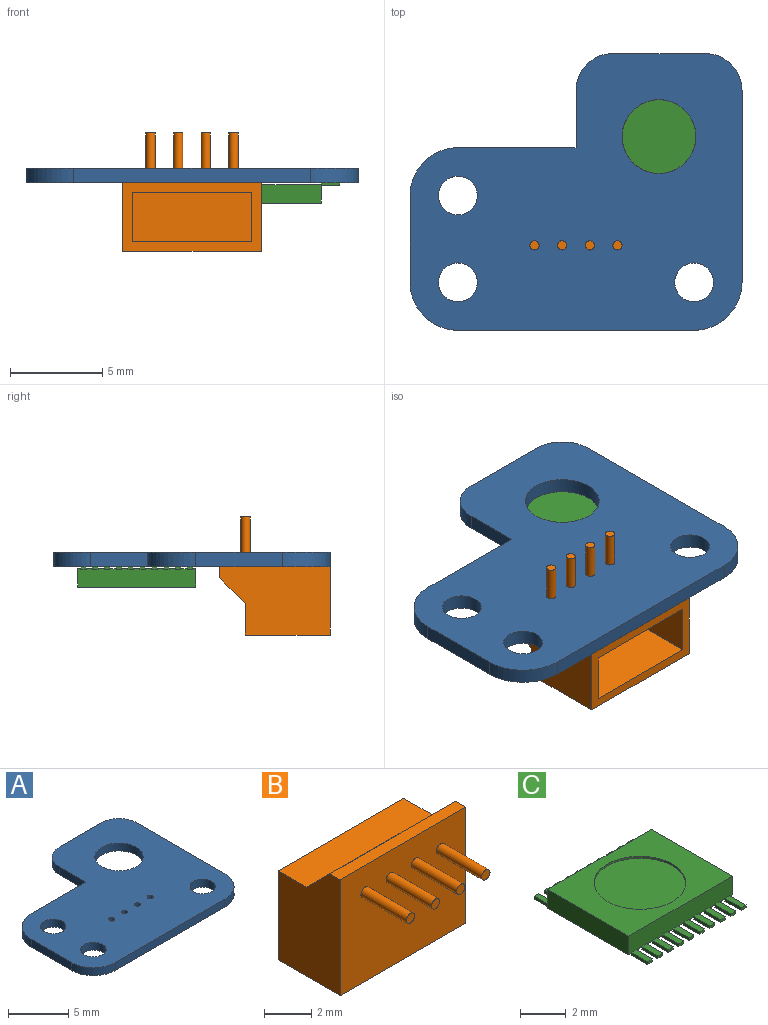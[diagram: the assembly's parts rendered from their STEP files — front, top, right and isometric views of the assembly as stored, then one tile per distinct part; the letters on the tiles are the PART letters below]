
ASSEMBLY  parts=3 mates=3
PART A: 21 faces, bbox 18x15x0.8 mm
  f0: plane 5x0.8mm, normal (0,1,0), area 4mm2, adj f4,f5,f19,f20
  f1: plane 4.7x0.8mm, normal (-1,0,0), area 3.8mm2, adj f4,f5,f16,f17
  f2: plane 12.8x0.8mm, normal (0,-1,0), area 10.2mm2, adj f4,f5,f17,f18
  f3: plane 10.4x0.8mm, normal (1,0,0), area 8.3mm2, adj f4,f5,f18,f20
  f4: plane 18x15mm, normal (0,0,1), area 194.3mm2, adj f0,f1,f2,f3,f6,f7,f8,f9
  f5: plane 18x15mm, normal (0,0,-1), area 194.3mm2, adj f0,f1,f2,f3,f6,f7,f8,f9
  f6: cylinder r=0.25mm len=0.8mm, axis (0,0,-1), area 1.3mm2, adj f4,f5
  f7: cylinder r=0.25mm len=0.8mm, axis (0,0,-1), area 1.3mm2, adj f4,f5
  f8: cylinder r=0.25mm len=0.8mm, axis (0,0,-1), area 1.3mm2, adj f4,f5
  f9: cylinder r=0.25mm len=0.8mm, axis (0,0,-1), area 1.3mm2, adj f4,f5
  f10: cylinder r=1.05mm len=2.1mm, axis (0,0,1), area 5.3mm2, adj f4,f5
  f11: cylinder r=1.05mm len=2.1mm, axis (0,0,1), area 5.3mm2, adj f4,f5
  f12: cylinder r=1.05mm len=2.1mm, axis (0,0,1), area 5.3mm2, adj f4,f5
  f13: plane 6.4x0.8mm, normal (0,1,0), area 5.1mm2, adj f4,f5,f14,f16
  f14: plane 3.1x0.8mm, normal (-1,0,0), area 2.5mm2, adj f4,f5,f13,f19
  f15: cylinder r=2mm len=4mm, axis (0,0,-1), area 10.1mm2, adj f4,f5
  f16: cylinder r=2.6mm len=2.6mm, axis (0,0,-1), area 3.3mm2, adj f1,f4,f5,f13
  f17: cylinder r=2.6mm len=2.6mm, axis (0,0,1), area 3.3mm2, adj f1,f2,f4,f5
  f18: cylinder r=2.6mm len=2.6mm, axis (0,0,-1), area 3.3mm2, adj f2,f3,f4,f5
  f19: cylinder r=2mm len=2mm, axis (0,0,1), area 2.5mm2, adj f0,f4,f5,f14
  f20: cylinder r=2mm len=2mm, axis (0,0,1), area 2.5mm2, adj f0,f3,f4,f5
PART B: 21 faces, bbox 7.5x6.4x6 mm
  f0: plane 7.5x3.7mm, normal (0,0,-1), area 10.2mm2, adj f2,f3,f4,f5,f8,f9,f10,f11
  f1: plane 7.5x1.7mm, normal (0,0,1), area 12.7mm2, adj f2,f4,f5,f7
  f2: plane 6x3.7mm, normal (-1,0,0), area 18.8mm2, adj f0,f1,f3,f5,f6,f7
  f3: plane 7.5x6mm, normal (0,-1,0), area 44.2mm2, adj f0,f2,f4,f6,f13,f15,f17,f19
  f4: plane 6x3.7mm, normal (1,0,0), area 18.8mm2, adj f0,f1,f3,f5,f6,f7
  f5: plane 7.5x4.6mm, normal (0,1,0), area 34.5mm2, adj f0,f1,f2,f4
  f6: plane 7.5x0.6mm, normal (0,0,1), area 4.5mm2, adj f2,f3,f4,f7
  f7: plane 7.5x1.4mm, normal (0,0.71,0.71), area 14.8mm2, adj f1,f2,f4,f6
  f8: plane 4.1x2.7mm, normal (-1,0,0), area 11.1mm2, adj f0,f9,f11,f12
  f9: plane 6.5x4.1mm, normal (0,1,0), area 26.7mm2, adj f0,f8,f10,f12
  f10: plane 4.1x2.7mm, normal (1,0,0), area 11.1mm2, adj f0,f9,f11,f12
  f11: plane 6.5x4.1mm, normal (0,-1,0), area 26.7mm2, adj f0,f8,f10,f12
  f12: plane 6.5x2.7mm, normal (0,0,-1), area 17.6mm2, adj f8,f9,f10,f11
  f13: cylinder r=0.25mm len=2.7mm, axis (0,1,0), area 4.2mm2, adj f3,f14
  f14: plane 0.5x0.5mm, normal (0,-1,0), area 0.2mm2, adj f13
  f15: cylinder r=0.25mm len=2.7mm, axis (0,1,0), area 4.2mm2, adj f3,f16
  f16: plane 0.5x0.5mm, normal (0,-1,0), area 0.2mm2, adj f15
  f17: cylinder r=0.25mm len=2.7mm, axis (0,1,0), area 4.2mm2, adj f3,f18
  f18: plane 0.5x0.5mm, normal (0,-1,0), area 0.2mm2, adj f17
  f19: cylinder r=0.25mm len=2.7mm, axis (0,1,0), area 4.2mm2, adj f3,f20
  f20: plane 0.5x0.5mm, normal (0,-1,0), area 0.2mm2, adj f19
PART C: 128 faces, bbox 6.4x7x1.1 mm
  f0: plane 1x0.3mm, normal (0,0,-1), area 0.3mm2, adj f41,f42,f44,f116
  f1: plane 1x0.3mm, normal (0,0,-1), area 0.3mm2, adj f37,f38,f40,f117
  f2: plane 1x0.3mm, normal (0,0,-1), area 0.3mm2, adj f33,f34,f36,f118
  f3: plane 1x0.3mm, normal (0,0,-1), area 0.3mm2, adj f29,f30,f32,f119
  f4: plane 1x0.3mm, normal (0,0,-1), area 0.3mm2, adj f25,f26,f28,f120
  f5: plane 1x0.3mm, normal (0,0,-1), area 0.3mm2, adj f45,f46,f48,f121
  f6: plane 1x0.3mm, normal (0,0,-1), area 0.3mm2, adj f49,f50,f52,f122
  f7: plane 1x0.3mm, normal (0,0,-1), area 0.3mm2, adj f53,f54,f56,f123
  f8: plane 1x0.3mm, normal (0,0,-1), area 0.3mm2, adj f57,f58,f60,f124
  f9: plane 1x0.3mm, normal (0,0,-1), area 0.3mm2, adj f101,f102,f104,f105
  f10: plane 1x0.3mm, normal (0,0,-1), area 0.3mm2, adj f97,f98,f100,f114
  f11: plane 1x0.3mm, normal (0,0,-1), area 0.3mm2, adj f93,f94,f96,f113
  f12: plane 1x0.3mm, normal (0,0,-1), area 0.3mm2, adj f89,f90,f92,f112
  f13: plane 1x0.3mm, normal (0,0,-1), area 0.3mm2, adj f85,f86,f88,f111
  f14: plane 1x0.3mm, normal (0,0,-1), area 0.3mm2, adj f65,f66,f68,f110
  f15: plane 1x0.3mm, normal (0,0,-1), area 0.3mm2, adj f69,f70,f72,f109
  f16: plane 1x0.3mm, normal (0,0,-1), area 0.3mm2, adj f73,f74,f76,f108
  f17: plane 1x0.3mm, normal (0,0,-1), area 0.3mm2, adj f77,f78,f80,f107
  f18: plane 1x0.3mm, normal (0,0,-1), area 0.3mm2, adj f81,f82,f84,f106
  f19: plane 6.4x1mm, normal (0,1,0), area 6.3mm2, adj f20,f22,f23,f65,f66,f67,f69,f70
  f20: plane 5x1mm, normal (-1,0,0), area 5mm2, adj f19,f21,f23,f125
  f21: plane 6.4x1mm, normal (0,-1,0), area 6.3mm2, adj f20,f22,f23,f25,f26,f27,f29,f30
  f22: plane 5x1mm, normal (1,0,0), area 5mm2, adj f19,f21,f23,f125
  f23: plane 6.4x5mm, normal (0,0,1), area 19.4mm2, adj f19,f20,f21,f22,f126
  f24: plane 1x0.3mm, normal (0,0,-1), area 0.3mm2, adj f61,f62,f64,f115
  f25: plane 1x0.15mm, normal (-1,0,0), area 0.1mm2, adj f4,f21,f27,f28,f120
  f26: plane 1x0.15mm, normal (1,0,0), area 0.1mm2, adj f4,f21,f27,f28,f120
  f27: plane 1x0.3mm, normal (0,0,1), area 0.3mm2, adj f21,f25,f26,f28
  f28: plane 0.3x0.15mm, normal (0,-1,0), area 0mm2, adj f4,f25,f26,f27
  f29: plane 1x0.15mm, normal (-1,0,0), area 0.1mm2, adj f3,f21,f31,f32,f119
  f30: plane 1x0.15mm, normal (1,0,0), area 0.1mm2, adj f3,f21,f31,f32,f119
  f31: plane 1x0.3mm, normal (0,0,1), area 0.3mm2, adj f21,f29,f30,f32
  f32: plane 0.3x0.15mm, normal (0,-1,0), area 0mm2, adj f3,f29,f30,f31
  f33: plane 1x0.15mm, normal (-1,0,0), area 0.1mm2, adj f2,f21,f35,f36,f118
  f34: plane 1x0.15mm, normal (1,0,0), area 0.1mm2, adj f2,f21,f35,f36,f118
  f35: plane 1x0.3mm, normal (0,0,1), area 0.3mm2, adj f21,f33,f34,f36
  f36: plane 0.3x0.15mm, normal (0,-1,0), area 0mm2, adj f2,f33,f34,f35
  f37: plane 1x0.15mm, normal (-1,0,0), area 0.1mm2, adj f1,f21,f39,f40,f117
  f38: plane 1x0.15mm, normal (1,0,0), area 0.1mm2, adj f1,f21,f39,f40,f117
  f39: plane 1x0.3mm, normal (0,0,1), area 0.3mm2, adj f21,f37,f38,f40
  f40: plane 0.3x0.15mm, normal (0,-1,0), area 0mm2, adj f1,f37,f38,f39
  f41: plane 1x0.15mm, normal (-1,0,0), area 0.1mm2, adj f0,f21,f43,f44,f116
  f42: plane 1x0.15mm, normal (1,0,0), area 0.1mm2, adj f0,f21,f43,f44,f116
  f43: plane 1x0.3mm, normal (0,0,1), area 0.3mm2, adj f21,f41,f42,f44
  f44: plane 0.3x0.15mm, normal (0,-1,0), area 0mm2, adj f0,f41,f42,f43
  f45: plane 1x0.15mm, normal (-1,0,0), area 0.1mm2, adj f5,f21,f47,f48,f121
  f46: plane 1x0.15mm, normal (1,0,0), area 0.1mm2, adj f5,f21,f47,f48,f121
  f47: plane 1x0.3mm, normal (0,0,1), area 0.3mm2, adj f21,f45,f46,f48
  f48: plane 0.3x0.15mm, normal (0,-1,0), area 0mm2, adj f5,f45,f46,f47
  f49: plane 1x0.15mm, normal (-1,0,0), area 0.1mm2, adj f6,f21,f51,f52,f122
  f50: plane 1x0.15mm, normal (1,0,0), area 0.1mm2, adj f6,f21,f51,f52,f122
  f51: plane 1x0.3mm, normal (0,0,1), area 0.3mm2, adj f21,f49,f50,f52
  f52: plane 0.3x0.15mm, normal (0,-1,0), area 0mm2, adj f6,f49,f50,f51
  f53: plane 1x0.15mm, normal (-1,0,0), area 0.1mm2, adj f7,f21,f55,f56,f123
  f54: plane 1x0.15mm, normal (1,0,0), area 0.1mm2, adj f7,f21,f55,f56,f123
  f55: plane 1x0.3mm, normal (0,0,1), area 0.3mm2, adj f21,f53,f54,f56
  f56: plane 0.3x0.15mm, normal (0,-1,0), area 0mm2, adj f7,f53,f54,f55
  f57: plane 1x0.15mm, normal (-1,0,0), area 0.1mm2, adj f8,f21,f59,f60,f124
  f58: plane 1x0.15mm, normal (1,0,0), area 0.1mm2, adj f8,f21,f59,f60,f124
  f59: plane 1x0.3mm, normal (0,0,1), area 0.3mm2, adj f21,f57,f58,f60
  f60: plane 0.3x0.15mm, normal (0,-1,0), area 0mm2, adj f8,f57,f58,f59
  f61: plane 1x0.15mm, normal (-1,0,0), area 0.1mm2, adj f21,f24,f63,f64,f115
  f62: plane 1x0.15mm, normal (1,0,0), area 0.1mm2, adj f21,f24,f63,f64,f115
  f63: plane 1x0.3mm, normal (0,0,1), area 0.3mm2, adj f21,f61,f62,f64
  f64: plane 0.3x0.15mm, normal (0,-1,0), area 0mm2, adj f24,f61,f62,f63
  f65: plane 1x0.15mm, normal (1,0,0), area 0.1mm2, adj f14,f19,f67,f68,f110
  f66: plane 1x0.15mm, normal (-1,0,0), area 0.1mm2, adj f14,f19,f67,f68,f110
  f67: plane 1x0.3mm, normal (0,0,1), area 0.3mm2, adj f19,f65,f66,f68
  f68: plane 0.3x0.15mm, normal (0,1,0), area 0mm2, adj f14,f65,f66,f67
  f69: plane 1x0.15mm, normal (1,0,0), area 0.1mm2, adj f15,f19,f71,f72,f109
  f70: plane 1x0.15mm, normal (-1,0,0), area 0.1mm2, adj f15,f19,f71,f72,f109
  f71: plane 1x0.3mm, normal (0,0,1), area 0.3mm2, adj f19,f69,f70,f72
  f72: plane 0.3x0.15mm, normal (0,1,0), area 0mm2, adj f15,f69,f70,f71
  f73: plane 1x0.15mm, normal (1,0,0), area 0.1mm2, adj f16,f19,f75,f76,f108
  f74: plane 1x0.15mm, normal (-1,0,0), area 0.1mm2, adj f16,f19,f75,f76,f108
  f75: plane 1x0.3mm, normal (0,0,1), area 0.3mm2, adj f19,f73,f74,f76
  f76: plane 0.3x0.15mm, normal (0,1,0), area 0mm2, adj f16,f73,f74,f75
  f77: plane 1x0.15mm, normal (1,0,0), area 0.1mm2, adj f17,f19,f79,f80,f107
  f78: plane 1x0.15mm, normal (-1,0,0), area 0.1mm2, adj f17,f19,f79,f80,f107
  f79: plane 1x0.3mm, normal (0,0,1), area 0.3mm2, adj f19,f77,f78,f80
  f80: plane 0.3x0.15mm, normal (0,1,0), area 0mm2, adj f17,f77,f78,f79
  f81: plane 1x0.15mm, normal (1,0,0), area 0.1mm2, adj f18,f19,f83,f84,f106
  f82: plane 1x0.15mm, normal (-1,0,0), area 0.1mm2, adj f18,f19,f83,f84,f106
  f83: plane 1x0.3mm, normal (0,0,1), area 0.3mm2, adj f19,f81,f82,f84
  f84: plane 0.3x0.15mm, normal (0,1,0), area 0mm2, adj f18,f81,f82,f83
  f85: plane 1x0.15mm, normal (1,0,0), area 0.1mm2, adj f13,f19,f87,f88,f111
  f86: plane 1x0.15mm, normal (-1,0,0), area 0.1mm2, adj f13,f19,f87,f88,f111
  f87: plane 1x0.3mm, normal (0,0,1), area 0.3mm2, adj f19,f85,f86,f88
  f88: plane 0.3x0.15mm, normal (0,1,0), area 0mm2, adj f13,f85,f86,f87
  f89: plane 1x0.15mm, normal (1,0,0), area 0.1mm2, adj f12,f19,f91,f92,f112
  f90: plane 1x0.15mm, normal (-1,0,0), area 0.1mm2, adj f12,f19,f91,f92,f112
  f91: plane 1x0.3mm, normal (0,0,1), area 0.3mm2, adj f19,f89,f90,f92
  f92: plane 0.3x0.15mm, normal (0,1,0), area 0mm2, adj f12,f89,f90,f91
  f93: plane 1x0.15mm, normal (1,0,0), area 0.1mm2, adj f11,f19,f95,f96,f113
  f94: plane 1x0.15mm, normal (-1,0,0), area 0.1mm2, adj f11,f19,f95,f96,f113
  f95: plane 1x0.3mm, normal (0,0,1), area 0.3mm2, adj f19,f93,f94,f96
  f96: plane 0.3x0.15mm, normal (0,1,0), area 0mm2, adj f11,f93,f94,f95
  f97: plane 1x0.15mm, normal (1,0,0), area 0.1mm2, adj f10,f19,f99,f100,f114
  f98: plane 1x0.15mm, normal (-1,0,0), area 0.1mm2, adj f10,f19,f99,f100,f114
  f99: plane 1x0.3mm, normal (0,0,1), area 0.3mm2, adj f19,f97,f98,f100
  f100: plane 0.3x0.15mm, normal (0,1,0), area 0mm2, adj f10,f97,f98,f99
  f101: plane 1x0.15mm, normal (1,0,0), area 0.1mm2, adj f9,f19,f103,f104,f105
  f102: plane 1x0.15mm, normal (-1,0,0), area 0.1mm2, adj f9,f19,f103,f104,f105
  f103: plane 1x0.3mm, normal (0,0,1), area 0.3mm2, adj f19,f101,f102,f104
  f104: plane 0.3x0.15mm, normal (0,1,0), area 0mm2, adj f9,f101,f102,f103
  f105: plane 0.3x0.1mm, normal (0,-1,0), area 0mm2, adj f9,f101,f102,f125
  f106: plane 0.3x0.1mm, normal (0,-1,0), area 0mm2, adj f18,f81,f82,f125
  f107: plane 0.3x0.1mm, normal (0,-1,0), area 0mm2, adj f17,f77,f78,f125
  f108: plane 0.3x0.1mm, normal (0,-1,0), area 0mm2, adj f16,f73,f74,f125
  f109: plane 0.3x0.1mm, normal (0,-1,0), area 0mm2, adj f15,f69,f70,f125
  f110: plane 0.3x0.1mm, normal (0,-1,0), area 0mm2, adj f14,f65,f66,f125
  f111: plane 0.3x0.1mm, normal (0,-1,0), area 0mm2, adj f13,f85,f86,f125
  f112: plane 0.3x0.1mm, normal (0,-1,0), area 0mm2, adj f12,f89,f90,f125
  f113: plane 0.3x0.1mm, normal (0,-1,0), area 0mm2, adj f11,f93,f94,f125
  f114: plane 0.3x0.1mm, normal (0,-1,0), area 0mm2, adj f10,f97,f98,f125
  f115: plane 0.3x0.1mm, normal (0,1,0), area 0mm2, adj f24,f61,f62,f125
  f116: plane 0.3x0.1mm, normal (0,1,0), area 0mm2, adj f0,f41,f42,f125
  f117: plane 0.3x0.1mm, normal (0,1,0), area 0mm2, adj f1,f37,f38,f125
  f118: plane 0.3x0.1mm, normal (0,1,0), area 0mm2, adj f2,f33,f34,f125
  f119: plane 0.3x0.1mm, normal (0,1,0), area 0mm2, adj f3,f29,f30,f125
  f120: plane 0.3x0.1mm, normal (0,1,0), area 0mm2, adj f4,f25,f26,f125
  f121: plane 0.3x0.1mm, normal (0,1,0), area 0mm2, adj f5,f45,f46,f125
  f122: plane 0.3x0.1mm, normal (0,1,0), area 0mm2, adj f6,f49,f50,f125
  f123: plane 0.3x0.1mm, normal (0,1,0), area 0mm2, adj f7,f53,f54,f125
  f124: plane 0.3x0.1mm, normal (0,1,0), area 0mm2, adj f8,f57,f58,f125
  f125: plane 6.4x5mm, normal (0,0,-1), area 32mm2, adj f19,f20,f21,f22,f105,f106,f107,f108
  f126: cylinder r=2mm len=4mm, axis (0,0,1), area 1.3mm2, adj f23,f127
  f127: plane 4x4mm, normal (0,0,1), area 12.6mm2, adj f126
PLACE A t=(0,-0.03,0)mm
PLACE B rot(axis=(-1,0,0),90deg) t=(5.25,-0.03,0)mm
PLACE C rot(axis=(-0.71,-0.71,0),180deg) t=(11,7.27,0)mm
MATE revolute B.f19 <-> A.f6  axis (0,0,1) through (11.25,4.57,0)mm
MATE fastened C.f126 <-> A.f15  axis (0,0,-1) through (13.5,10.47,-1.1)mm
MATE revolute B.f13 <-> A.f9  axis (0,0,1) through (6.75,4.57,0)mm
